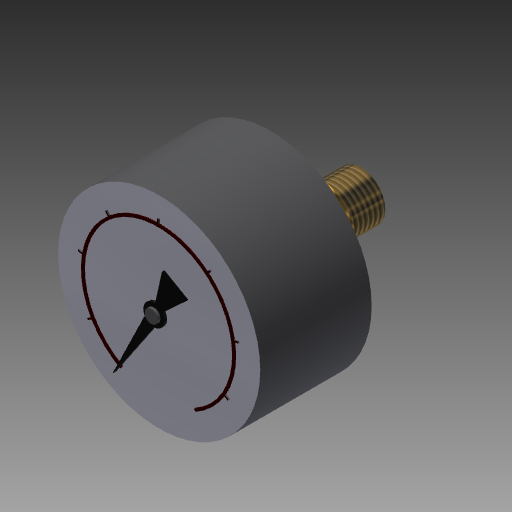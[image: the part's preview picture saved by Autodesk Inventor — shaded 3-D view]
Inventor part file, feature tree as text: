
AUTODESK INVENTOR PART (.ipt)
format: ipt  version: 2017.1 (Build 211199000, 199)  size: 186,880 bytes
history: native  units: mm
features: imported_body x1, thread x1
ambient origin geometry x8: Origin, YZ Plane, XZ Plane, XY Plane, X Axis, Y Axis, Z Axis, Center Point
bodies: Solid1 (feature_tree)
feature tree (2):
  imported_body  "Base1"
  thread  "Thread1"  [1 undecoded]
note: 1 required parameter value undecoded (feature->parameter linkage not recoverable at this tier; creation-order binding heuristic only, values carry confidence <= 0.55)
